# Revit family: v2_FP-Revit20-en-WD1871HG1-WasherDryer-0-90004397A-AU-NZ
name_source: partatom
category: Specialty Equipment
units: mm (PartAtom-declared; Revit-internal decimal feet)

## family parameters
Always vertical = Yes
Cut with Voids When Loaded = Yes
OmniClass Number = 23.45.70.11.11.14
OmniClass Title = Clothes Dryers
Part Type = Normal
Room Calculation Point = No
Round Connector Dimension = Use Diameter
Shared = Yes
Work Plane-Based = No

## types (2) — shared parameters
Cavity - Depth = 828 mm  [stored 2.71654 ft]
Cavity - Width = 726 mm  [stored 2.38189 ft]
Clearance - Above = 20 mm  [stored 0.0656168 ft]
Connector Description - Electrical = 230V, 50Hz, 10 A
Description = Heat Pump Washer Dryer Combi
Manufacturer = Fisher & Paykel Appliances
Material - Body = Fisher & Paykel - Grey
Material - Glass = Fisher & Paykel - Glass, Black
Material - Trim = Fisher & Paykel - Steel, Chrome Plated
Model = WD1871HG1
Product - Depth = 813 mm
Product - Width = 711 mm  [stored 2.33268 ft]
URL = www.fisherpaykel.com
Visibility - Clearance Required = Yes
zero-valued in all types: Default Elevation

## per-type parameters (varying)
| type | Material - Control Panel | Material - Display Panel | Material - Front |
| WD1871HG1 - Proud install | Fisher & Paykel - Aluminium, Dark | Fisher & Paykel - Display | Fisher & Paykel - Grey, Charcoal |
| WD1871HG1 - Flush install | Fisher & Paykel - Glass, Graphite | Fisher & Paykel - Black | Fisher & Paykel - Graphite |

note: [stored X ft] marks values corroborated as IEEE doubles in the binary element streams (Revit-internal decimal feet)

## geometry (parser evidence)
native form markers: Sweep x2
no freeform markers — native parametric forms only
